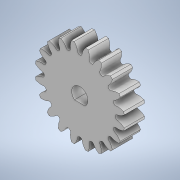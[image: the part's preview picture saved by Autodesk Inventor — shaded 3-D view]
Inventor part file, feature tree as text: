
AUTODESK INVENTOR PART (.ipt)
format: ipt  version: 2021 (Build 250183000, 183)  size: 256,000 bytes
history: native  units: mm
features: extrude x3, sketch x2, pattern_circular x1
ambient origin geometry x8: Origin, YZ Plane, XZ Plane, XY Plane, X Axis, Y Axis, Z Axis, Center Point
bodies: Solid1 (feature_tree)
feature tree (6):
  sketch  "Sketch1"  dims[d0=10.0mm d1=0.0mm d2=0.0mm d3=0.0mm]
  extrude  "Extrusion1"  TaperAngle=0.0deg  [1 undecoded]
  extrude  "Extrusion2"  Depth=8.0mm
  pattern_circular  "Circular Pattern1"  [2 undecoded]
  extrude  "Extrusion3"  Depth=5.29mm
  sketch  "Sketch3"  dims[d4=200.0mm d5=360.0deg d7=8.0mm d8=0.0mm d9=0.0mm d18=5.29mm d19=14.448666mm d20=8.48363mm d21=8.483061mm d10=0.15mm d11=0.25mm d12=0.375mm d13=14.3117mm d14=0.75mm d15=20.594885mm d16=0.0625mm d17=0.75mm]
note: 3 required parameter values undecoded (feature->parameter linkage not recoverable at this tier; creation-order binding heuristic only, values carry confidence <= 0.55)
